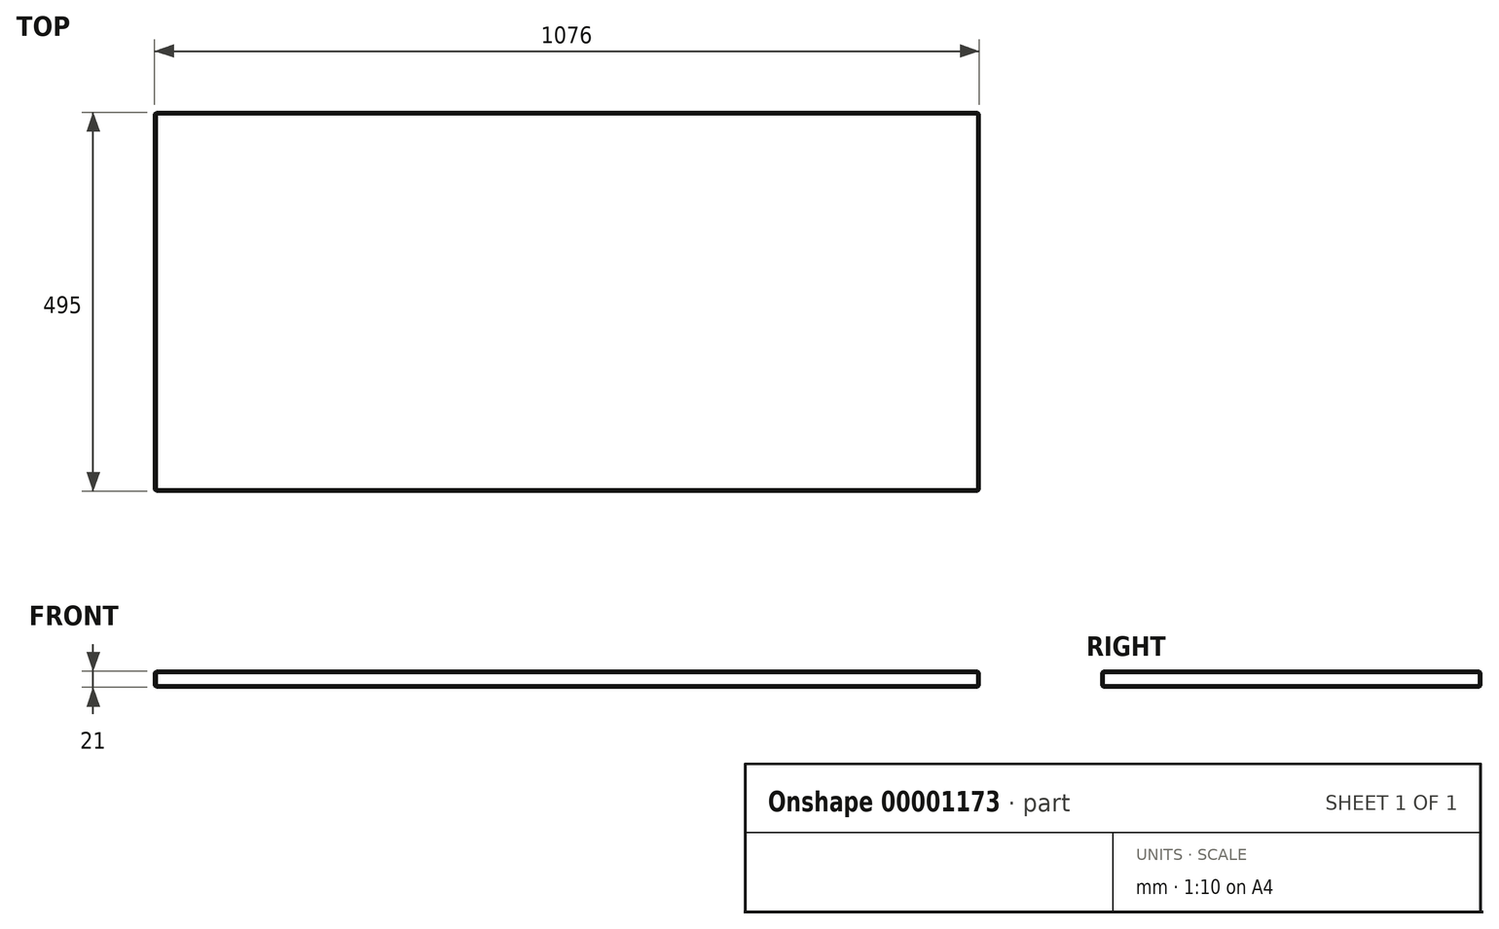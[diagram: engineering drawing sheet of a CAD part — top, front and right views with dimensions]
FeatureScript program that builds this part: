
annotation { "Feature Type Name" : "Feature", "Feature Type Description" : "" }
export const myFeature = defineFeature(function(context is Context, id is Id, definition is map)
    precondition{}
    {
        {
            var Q0;
            Q0=qCreatedBy(makeId("Top.planeOp"),FACE);
            var sketch = newSketch(context, id + "F0", { "sketchPlane" : qUnion([Q0])});
            skLineSegment(sketch, "E0.bottom", {"start": v(0, 0) * mm, "end": v(1076, 0) * mm});
            skLineSegment(sketch, "E0.top", {"start": v(0, 495) * mm, "end": v(1076, 495) * mm});
            skLineSegment(sketch, "E0.left", {"start": v(0, 0) * mm, "end": v(0, 495) * mm});
            skLineSegment(sketch, "E0.right", {"start": v(1076, 0) * mm, "end": v(1076, 495) * mm});
            skSolve(sketch);
        }
        {
            var Q0;
            Q0 = qSketchRegion(id + "F0", true);
            extrude(context, id + "F1", {"entities" : qUnion([Q0]), "depth" : 21 * mm});
        }
        {
            var Q0;
            Q0=makeQuery(id+"F1.opExtrude","CAP_FACE",FACE,{"disambiguationData":[OSD([sQuery(id+"F0.wireOp",EDGE,"E0.bottom"),sQuery(id+"F0.wireOp",EDGE,"E0.top"),sQuery(id+"F0.wireOp",EDGE,"E0.left"),sQuery(id+"F0.wireOp",EDGE,"E0.right")])],"isStart":false});
            var Q1;
            Q1=makeQuery(id+"F1.opExtrude","CAP_FACE",FACE,{"disambiguationData":[OSD([sQuery(id+"F0.wireOp",EDGE,"E0.bottom"),sQuery(id+"F0.wireOp",EDGE,"E0.top"),sQuery(id+"F0.wireOp",EDGE,"E0.left"),sQuery(id+"F0.wireOp",EDGE,"E0.right")])],"isStart":true});
            var Q2;
            Q2=makeQuery(id+"F1.opExtrude","SWEPT_EDGE",EDGE,{"disambiguationData":[OSD([sQuery(id+"F0.wireOp",EDGE,"E0.bottom"),sQuery(id+"F0.wireOp",EDGE,"E0.right")])]});
            var Q3;
            Q3=makeQuery(id+"F1.opExtrude","SWEPT_EDGE",EDGE,{"disambiguationData":[OSD([sQuery(id+"F0.wireOp",EDGE,"E0.bottom"),sQuery(id+"F0.wireOp",EDGE,"E0.left")])]});
            var Q4;
            Q4=makeQuery(id+"F1.opExtrude","SWEPT_EDGE",EDGE,{"disambiguationData":[OSD([sQuery(id+"F0.wireOp",EDGE,"E0.top"),sQuery(id+"F0.wireOp",EDGE,"E0.left")])]});
            var Q5;
            Q5=makeQuery(id+"F1.opExtrude","SWEPT_EDGE",EDGE,{"disambiguationData":[OSD([sQuery(id+"F0.wireOp",EDGE,"E0.top"),sQuery(id+"F0.wireOp",EDGE,"E0.right")])]});
            chamfer(context, id + "F2", {"entities" : qUnion([Q0, Q1, Q2, Q3, Q4, Q5]), "width" : 2 * mm, "tangentPropagation" : true});
        }
    });
